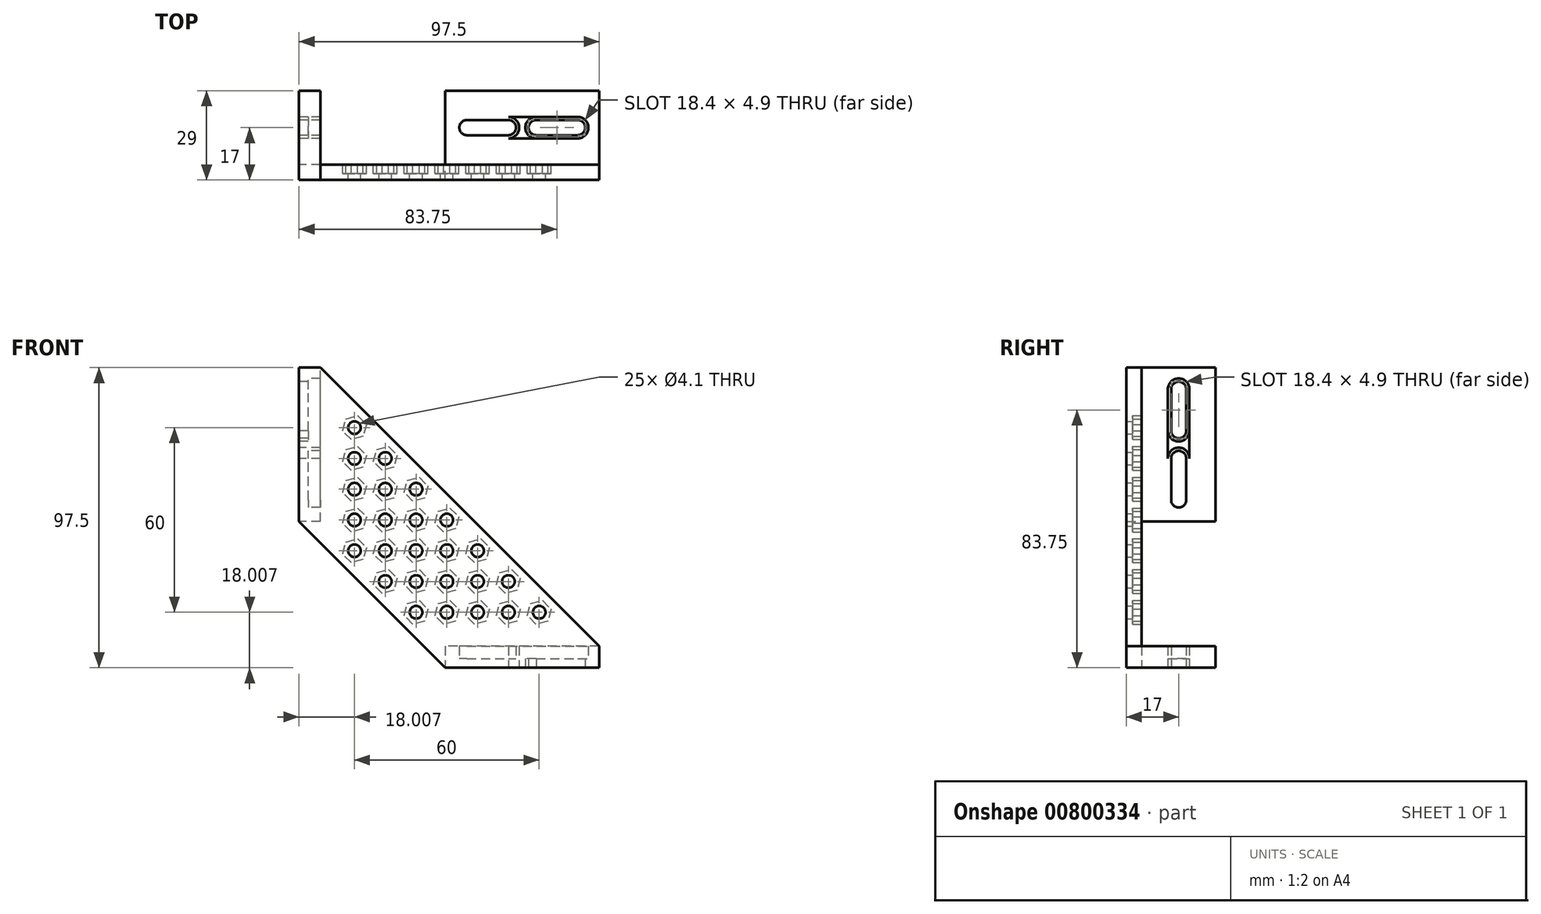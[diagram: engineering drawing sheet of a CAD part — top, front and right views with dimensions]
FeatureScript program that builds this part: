
annotation { "Feature Type Name" : "Feature", "Feature Type Description" : "" }
export const myFeature = defineFeature(function(context is Context, id is Id, definition is map)
    precondition{}
    {
        {
            var Q0;
            Q0=qCreatedBy(makeId("Top.planeOp"),FACE);
            var sketch = newSketch(context, id + "F0", { "sketchPlane" : qUnion([Q0])});
            skLineSegment(sketch, "E0.left", {"start": v(-21, 12) * mm, "end": v(-21, -12) * mm});
            skPoint(sketch, "E0.middle", {"position": v(0, 0) * mm});
            skLineSegment(sketch, "E1", {"start": v(-14, 12) * mm, "end": v(-14, -12) * mm, "construction": true});
            skPoint(sketch, "E2", {"position": v(-14, -8) * mm});
            skPoint(sketch, "E3", {"position": v(0, -8) * mm});
            skPoint(sketch, "E4", {"position": v(-14, 0) * mm});
            skArc(sketch, "E5", {"start": v(-14, -5.95) * mm, "mid": v(-16.05, -8) * mm, "end": v(-14, -10.05) * mm});
            skLineSegment(sketch, "E6", {"start": v(-14, -5.95) * mm, "end": v(0, -5.95) * mm});
            skLineSegment(sketch, "E7.MirrorCS", {"start": v(-14, -10.05) * mm, "end": v(0, -10.05) * mm});
            skArc(sketch, "E8", {"start": v(-14, -2.45) * mm, "mid": v(-16.45, 0) * mm, "end": v(-14, 2.45) * mm});
            skPoint(sketch, "E9.MirrorP", {"position": v(-14, 2.45) * mm});
            skLineSegment(sketch, "E10.MirrorCS", {"start": v(0, -12) * mm, "end": v(0, 12) * mm, "construction": true});
            skLineSegment(sketch, "E11", {"start": v(-21, -12) * mm, "end": v(0, -12) * mm});
            skLineSegment(sketch, "E12", {"start": v(-21, 0) * mm, "end": v(0, 0) * mm, "construction": true});
            skLineSegment(sketch, "E13", {"start": v(0, -8) * mm, "end": v(-21, -8) * mm, "construction": true});
            skPoint(sketch, "E13.endSnap0", {"position": v(-16.05, -8) * mm});
            skLineSegment(sketch, "E14", {"start": v(0, -12) * mm, "end": v(29, -12) * mm});
            skLineSegment(sketch, "E15", {"start": v(29, -12) * mm, "end": v(29, 12) * mm});
            skLineSegment(sketch, "E16", {"start": v(29, 12) * mm, "end": v(-21, 12) * mm});
            skLineSegment(sketch, "E17", {"start": v(22, 12) * mm, "end": v(22, -12) * mm, "construction": true});
            skLineSegment(sketch, "E18", {"start": v(0, -5.95) * mm, "end": v(22, -5.95) * mm});
            skLineSegment(sketch, "E19", {"start": v(0, -10.05) * mm, "end": v(22, -10.05) * mm});
            skLineSegment(sketch, "E20", {"start": v(22, 0) * mm, "end": v(0, 0) * mm, "construction": true});
            skLineSegment(sketch, "E21", {"start": v(0, -8) * mm, "end": v(22, -8) * mm, "construction": true});
            skArc(sketch, "E22", {"start": v(22, -2.45) * mm, "mid": v(24.45, 0) * mm, "end": v(22, 2.45) * mm});
            skArc(sketch, "E23", {"start": v(22, -10.05) * mm, "mid": v(24.05, -8) * mm, "end": v(22, -5.95) * mm});
            skLineSegment(sketch, "E24.MirrorCS", {"start": v(0, 5.95) * mm, "end": v(22, 5.95) * mm});
            skLineSegment(sketch, "E25.MirrorCS", {"start": v(0, 10.05) * mm, "end": v(22, 10.05) * mm});
            skLineSegment(sketch, "E26.MirrorCS", {"start": v(-14, 10.05) * mm, "end": v(0, 10.05) * mm});
            skLineSegment(sketch, "E27.MirrorCS", {"start": v(-14, 5.95) * mm, "end": v(0, 5.95) * mm});
            skArc(sketch, "E28.MirrorCS", {"start": v(-14, 5.95) * mm, "mid": v(-16.05, 8) * mm, "end": v(-14, 10.05) * mm});
            skArc(sketch, "E29.MirrorCS", {"start": v(22, 10.05) * mm, "mid": v(24.05, 8) * mm, "end": v(22, 5.95) * mm});
            skArc(sketch, "E30.0", {"start": v(-14, -4.5) * mm, "mid": v(-17.5, -8) * mm, "end": v(-14, -11.5) * mm});
            skLineSegment(sketch, "E30.1", {"start": v(4.6, -4.5) * mm, "end": v(22, -4.5) * mm});
            skArc(sketch, "E30.2", {"start": v(22, -11.5) * mm, "mid": v(25.5, -8) * mm, "end": v(22, -4.5) * mm});
            skLineSegment(sketch, "E30.3", {"start": v(-14, -4.5) * mm, "end": v(4.6, -4.5) * mm});
            skLineSegment(sketch, "E30.4", {"start": v(5, -11.5) * mm, "end": v(22, -11.5) * mm});
            skLineSegment(sketch, "E30.5", {"start": v(-14, -11.5) * mm, "end": v(5, -11.5) * mm});
            skArc(sketch, "E31.0", {"start": v(-14, 4.5) * mm, "mid": v(-17.5, 8) * mm, "end": v(-14, 11.5) * mm});
            skLineSegment(sketch, "E31.1", {"start": v(-3, 11.5) * mm, "end": v(22, 11.5) * mm});
            skArc(sketch, "E31.2", {"start": v(22, 11.5) * mm, "mid": v(25.5, 8) * mm, "end": v(22, 4.5) * mm});
            skLineSegment(sketch, "E31.3", {"start": v(-14, 11.5) * mm, "end": v(-3, 11.5) * mm});
            skLineSegment(sketch, "E31.4", {"start": v(-3, 4.5) * mm, "end": v(22, 4.5) * mm});
            skLineSegment(sketch, "E31.5", {"start": v(-14, 4.5) * mm, "end": v(-3, 4.5) * mm});
            skArc(sketch, "E32", {"start": v(-14, -3.5) * mm, "mid": v(-17.5, 0) * mm, "end": v(-14, 3.5) * mm});
            skArc(sketch, "E33", {"start": v(22, -3.5) * mm, "mid": v(25.5, 0) * mm, "end": v(22, 3.5) * mm});
            skLineSegment(sketch, "E34", {"start": v(-14, 3.5) * mm, "end": v(22, 3.5) * mm});
            skLineSegment(sketch, "E35", {"start": v(22, -3.5) * mm, "end": v(-14, -3.5) * mm});
            skPoint(sketch, "E36", {"position": v(29, 0) * mm});
            skLineSegment(sketch, "E37", {"start": v(-14, 2.45) * mm, "end": v(-0.5, 2.45) * mm});
            skPoint(sketch, "E38", {"position": v(-0.5, 0) * mm});
            skPoint(sketch, "E39", {"position": v(8.5, 0) * mm});
            skArc(sketch, "E40", {"start": v(-0.5, -2.45) * mm, "mid": v(1.95, 0) * mm, "end": v(-0.5, 2.45) * mm});
            skLineSegment(sketch, "E41", {"start": v(-14, -2.45) * mm, "end": v(-0.5, -2.45) * mm});
            skArc(sketch, "E42", {"start": v(8.5, -2.45) * mm, "mid": v(6.05, 0) * mm, "end": v(8.5, 2.45) * mm});
            skLineSegment(sketch, "E43", {"start": v(8.5, 2.45) * mm, "end": v(22, 2.45) * mm});
            skLineSegment(sketch, "E44", {"start": v(22, -2.45) * mm, "end": v(8.5, -2.45) * mm});
            skPoint(sketch, "E45", {"position": v(1.95, 0) * mm});
            skPoint(sketch, "E46", {"position": v(6.05, 0) * mm});
            skArc(sketch, "E47", {"start": v(-0.5, 3.5) * mm, "mid": v(3, 0) * mm, "end": v(-0.5, -3.5) * mm});
            skArc(sketch, "E48", {"start": v(8.5, 3.5) * mm, "mid": v(5, 0) * mm, "end": v(8.5, -3.5) * mm});
            skPoint(sketch, "E49", {"position": v(3, 0) * mm});
            skPoint(sketch, "E50", {"position": v(5, 0) * mm});
            skPoint(sketch, "E51", {"position": v(4, 3.5) * mm});
            skPoint(sketch, "E52", {"position": v(4, -3.5) * mm});
            skLineSegment(sketch, "E53", {"start": v(4, 12) * mm, "end": v(4, -12) * mm, "construction": true});
            skSolve(sketch);
        }
        {
            var Q0;
            Q0=makeQuery(id+"F0.imprint","IMPRINT",FACE,{"disambiguationData":[TD([[makeQuery(id+"F0.imprint","IMPRINT",EDGE,{"derivedFrom":sQuery(id+"F0.wireOp",EDGE,"E0.left")}),1.0]])]});
            var Q1;
            Q1=makeQuery(id+"F0.imprint","IMPRINT",FACE,{"disambiguationData":[TD([[makeQuery(id+"F0.imprint","IMPRINT",EDGE,{"derivedFrom":sQuery(id+"F0.wireOp",EDGE,"E5")}),1.0]])]});
            var Q2;
            Q2=makeQuery(id+"F0.imprint","IMPRINT",FACE,{"disambiguationData":[TD([[makeQuery(id+"F0.imprint","IMPRINT",EDGE,{"derivedFrom":sQuery(id+"F0.wireOp",EDGE,"E5")}),-1.0]])]});
            var Q3;
            Q3=makeQuery(id+"F0.imprint","IMPRINT",FACE,{"disambiguationData":[TD([[makeQuery(id+"F0.imprint","IMPRINT",EDGE,{"derivedFrom":sQuery(id+"F0.wireOp",EDGE,"E24.MirrorCS")}),-1.0]])]});
            var Q4;
            Q4=makeQuery(id+"F0.imprint","IMPRINT",FACE,{"disambiguationData":[TD([[makeQuery(id+"F0.imprint","IMPRINT",EDGE,{"derivedFrom":sQuery(id+"F0.wireOp",EDGE,"E24.MirrorCS")}),1.0]])]});
            var Q5;
            {var subQ0=sQuery(id+"F0.wireOp",EDGE,"E47");Q5=makeQuery(id+"F0.imprint","IMPRINT",FACE,{"disambiguationData":[TD([[makeQuery(id+"F0.imprint","IMPRINT",EDGE,{"derivedFrom":subQ0}),1.0]])]});}
            extrude(context, id + "F1", {"entities" : qUnion([Q0, Q1, Q2, Q3, Q4, Q5]), "depth" : 7 * mm, "offsetDistance" : 25 * mm});
        }
        {
            var Q0;
            Q0=makeQuery(id+"F0.imprint","IMPRINT",FACE,{"disambiguationData":[TD([[makeQuery(id+"F0.imprint","IMPRINT",EDGE,{"derivedFrom":sQuery(id+"F0.wireOp",EDGE,"E8")}),1.0]])]});
            var Q1;
            Q1=makeQuery(id+"F0.imprint","IMPRINT",FACE,{"disambiguationData":[TD([[makeQuery(id+"F0.imprint","IMPRINT",EDGE,{"derivedFrom":sQuery(id+"F0.wireOp",EDGE,"E22")}),-1.0]])]});
            extrude(context, id + "F2", {"entities" : qUnion([Q0, Q1]), "operationType" : NewBodyOperationType.ADD, "depth" : 3 * mm, "offsetDistance" : 25 * mm});
        }
        {
            var Q0;
            Q0=makeQuery(id+"F1.opExtrude","SWEPT_FACE",FACE,{"disambiguationData":[OSD([sQuery(id+"F0.wireOp",EDGE,"E0.left")])]});
            var sketch = newSketch(context, id + "F3", { "sketchPlane" : qUnion([Q0])});
            skLineSegment(sketch, "E54", {"start": v(-12, 3.5) * mm, "end": v(12, 3.5) * mm, "construction": true});
            skSolve(sketch);
        }
        {
            var Q0;
            Q0=makeQuery(id+"F1.opExtrude","SWEPT_BODY",BODY,{"disambiguationData":[OSD([sQuery(id+"F0.wireOp",EDGE,"E0.bottom"),sQuery(id+"F0.wireOp",EDGE,"E0.top"),sQuery(id+"F0.wireOp",EDGE,"E0.left"),sQuery(id+"F0.wireOp",EDGE,"E0.right"),sQuery(id+"F0.wireOp",EDGE,"rf366HtQ-3S43-huQP-rZQL-GLvETnePYKPt"),sQuery(id+"F0.wireOp",EDGE,"72d57c59-205e-4b86-9b7f-fefa83471a3c0.MirrorC"),sQuery(id+"F0.wireOp",EDGE,"3BxVGwLA-TLUy-tZVP-cH0U-NxRYkcQ5ksQi"),sQuery(id+"F0.wireOp",EDGE,"b526d6a5-a937-4610-9a53-f8e406b30c9d0.MirrorC"),sQuery(id+"F0.wireOp",EDGE,"71981b63-6e51-433c-862b-60b74b25135c0.MirrorC"),sQuery(id+"F0.wireOp",EDGE,"b5f8f83e-67df-48da-9f18-6f8bbd20fa1b0.MirrorC"),sQuery(id+"F0.wireOp",EDGE,"1DxgEhBs-8iCY-IMLj-HmtB-05ri525AO9wY"),sQuery(id+"F0.wireOp",EDGE,"NxLUD5A4-VjtB-lD8M-x3iM-VxBEk0lLSaKk"),sQuery(id+"F0.wireOp",EDGE,"3f1f5e11-1e70-4af8-87df-d7b5c765f6460.MirrorC")])]});
            var Q1;
            Q1=sQuery(id+"F3.wireOp",EDGE,"E54");
            transform(context, id + "F4", {"entities" : qUnion([Q0]), "transformType" : TransformType.ROTATION, "transformAxis" : qUnion([Q1]), "angle" : 90 * degree, "makeCopy" : true});
        }
        {
            var Q0;
            Q0=makeQuery(id+"F4.opPattern","COPY",FACE,{"derivedFrom":makeQuery(id+"F1.opExtrude","SWEPT_FACE",FACE,{"disambiguationData":[OSD([sQuery(id+"F0.wireOp",EDGE,"E0.left")])]}),"instanceName":"1"});
            var sketch = newSketch(context, id + "F5", { "sketchPlane" : qUnion([Q0])});
            skLineSegment(sketch, "E55", {"start": v(-21, -12) * mm, "end": v(-21, 12) * mm, "construction": true});
            skPoint(sketch, "E55.startSnap0", {"position": v(-21, -12) * mm});
            skSolve(sketch);
        }
        {
            var Q0;
            Q0=sQuery(id+"F5.wireOp",EDGE,"E55");
            cPlane(context, id + "F6", {"entities" : qUnion([Q0]), "cplaneType" : CPlaneType.LINE_ANGLE, "offset" : 25 * mm, "angle" : 90 * degree, "width" : 150 * mm, "height" : 150 * mm});
        }
        {
            var Q0;
            Q0=qCreatedBy(id+"F6.planeOp",FACE);
            var sketch = newSketch(context, id + "F7", { "sketchPlane" : qUnion([Q0])});
            skLineSegment(sketch, "E56", {"start": v(0, 3.5) * mm, "end": v(0, 53.5) * mm, "construction": true});
            skSolve(sketch);
        }
        {
            var Q0;
            Q0=makeQuery(id+"F4.opPattern","COPY",BODY,{"derivedFrom":makeQuery(id+"F1.opExtrude","SWEPT_BODY",BODY,{"disambiguationData":[OSD([sQuery(id+"F0.wireOp",EDGE,"E0.left"),sQuery(id+"F0.wireOp",EDGE,"E11"),sQuery(id+"F0.wireOp",EDGE,"E14"),sQuery(id+"F0.wireOp",EDGE,"E15"),sQuery(id+"F0.wireOp",EDGE,"E16"),sQuery(id+"F0.wireOp",EDGE,"2010bd3d-8bd0-4ab8-9feb-11eef9d441c0.0"),sQuery(id+"F0.wireOp",EDGE,"2010bd3d-8bd0-4ab8-9feb-11eef9d441c0.1"),sQuery(id+"F0.wireOp",EDGE,"2010bd3d-8bd0-4ab8-9feb-11eef9d441c0.2"),sQuery(id+"F0.wireOp",EDGE,"2010bd3d-8bd0-4ab8-9feb-11eef9d441c0.3"),sQuery(id+"F0.wireOp",EDGE,"2010bd3d-8bd0-4ab8-9feb-11eef9d441c0.4"),sQuery(id+"F0.wireOp",EDGE,"2010bd3d-8bd0-4ab8-9feb-11eef9d441c0.5")])]}),"instanceName":"1"});
            var Q1;
            Q1=sQuery(id+"F7.wireOp",EDGE,"E56");
            transform(context, id + "F8", {"entities" : qUnion([Q0]), "transformType" : TransformType.ROTATION, "transformAxis" : qUnion([Q1]), "angle" : 180 * degree, "makeCopy" : false});
        }
        {
            var Q0;
            Q0=makeQuery(id+"F4.opPattern","COPY",BODY,{"derivedFrom":makeQuery(id+"F1.opExtrude","SWEPT_BODY",BODY,{"disambiguationData":[OSD([sQuery(id+"F0.wireOp",EDGE,"E0.bottom"),sQuery(id+"F0.wireOp",EDGE,"E0.top"),sQuery(id+"F0.wireOp",EDGE,"E0.left"),sQuery(id+"F0.wireOp",EDGE,"E0.right"),sQuery(id+"F0.wireOp",EDGE,"rf366HtQ-3S43-huQP-rZQL-GLvETnePYKPt"),sQuery(id+"F0.wireOp",EDGE,"72d57c59-205e-4b86-9b7f-fefa83471a3c0.MirrorC"),sQuery(id+"F0.wireOp",EDGE,"3BxVGwLA-TLUy-tZVP-cH0U-NxRYkcQ5ksQi"),sQuery(id+"F0.wireOp",EDGE,"b526d6a5-a937-4610-9a53-f8e406b30c9d0.MirrorC"),sQuery(id+"F0.wireOp",EDGE,"71981b63-6e51-433c-862b-60b74b25135c0.MirrorC"),sQuery(id+"F0.wireOp",EDGE,"b5f8f83e-67df-48da-9f18-6f8bbd20fa1b0.MirrorC"),sQuery(id+"F0.wireOp",EDGE,"1DxgEhBs-8iCY-IMLj-HmtB-05ri525AO9wY"),sQuery(id+"F0.wireOp",EDGE,"NxLUD5A4-VjtB-lD8M-x3iM-VxBEk0lLSaKk"),sQuery(id+"F0.wireOp",EDGE,"3f1f5e11-1e70-4af8-87df-d7b5c765f6460.MirrorC")])]}),"instanceName":"1"});
            var Q1;
            Q1=qCreatedBy(makeId("Top.planeOp"),FACE);
            transform(context, id + "F9", {"entities" : qUnion([Q0]), "transformType" : TransformType.TRANSLATION_DISTANCE, "transformDirection" : qUnion([Q1]), "distance" : 44 * mm, "makeCopy" : false});
        }
        {
            var Q0;
            Q0=makeQuery(id+"F4.opPattern","COPY",BODY,{"derivedFrom":makeQuery(id+"F1.opExtrude","SWEPT_BODY",BODY,{"disambiguationData":[OSD([sQuery(id+"F0.wireOp",EDGE,"E0.bottom"),sQuery(id+"F0.wireOp",EDGE,"E0.top"),sQuery(id+"F0.wireOp",EDGE,"E0.left"),sQuery(id+"F0.wireOp",EDGE,"E0.right"),sQuery(id+"F0.wireOp",EDGE,"rf366HtQ-3S43-huQP-rZQL-GLvETnePYKPt"),sQuery(id+"F0.wireOp",EDGE,"72d57c59-205e-4b86-9b7f-fefa83471a3c0.MirrorC"),sQuery(id+"F0.wireOp",EDGE,"3BxVGwLA-TLUy-tZVP-cH0U-NxRYkcQ5ksQi"),sQuery(id+"F0.wireOp",EDGE,"b526d6a5-a937-4610-9a53-f8e406b30c9d0.MirrorC"),sQuery(id+"F0.wireOp",EDGE,"71981b63-6e51-433c-862b-60b74b25135c0.MirrorC"),sQuery(id+"F0.wireOp",EDGE,"b5f8f83e-67df-48da-9f18-6f8bbd20fa1b0.MirrorC"),sQuery(id+"F0.wireOp",EDGE,"1DxgEhBs-8iCY-IMLj-HmtB-05ri525AO9wY"),sQuery(id+"F0.wireOp",EDGE,"NxLUD5A4-VjtB-lD8M-x3iM-VxBEk0lLSaKk"),sQuery(id+"F0.wireOp",EDGE,"3f1f5e11-1e70-4af8-87df-d7b5c765f6460.MirrorC")])]}),"instanceName":"1"});
            var Q1;
            Q1=qCreatedBy(makeId("Right.planeOp"),FACE);
            transform(context, id + "F10", {"entities" : qUnion([Q0]), "transformType" : TransformType.TRANSLATION_DISTANCE, "transformDirection" : qUnion([Q1]), "distance" : 44 * mm, "oppositeDirection" : true, "makeCopy" : false});
        }
        {
            var Q0;
            Q0=sQuery(id+"F0.wireOp",VERTEX,"E0.left.end");
            var Q1;
            Q1=makeQuery(id+"F4.opPattern","COPY",VERTEX,{"derivedFrom":makeQuery(id+"F1.opExtrude","CAP_VERTEX",VERTEX,{"disambiguationData":[OSD([sQuery(id+"F0.wireOp",EDGE,"E0.left"),sQuery(id+"F0.wireOp",EDGE,"E16")])],"isStart":true}),"instanceName":"1"});
            var Q2;
            Q2=makeQuery(id+"F4.opPattern","COPY",VERTEX,{"derivedFrom":makeQuery(id+"F1.opExtrude","CAP_VERTEX",VERTEX,{"disambiguationData":[OSD([sQuery(id+"F0.wireOp",EDGE,"E0.left"),sQuery(id+"F0.wireOp",EDGE,"E16")])],"isStart":false}),"instanceName":"1"});
            cPlane(context, id + "F11", {"entities" : qUnion([Q0, Q1, Q2]), "cplaneType" : CPlaneType.THREE_POINT, "offset" : 25 * mm, "width" : 150 * mm, "height" : 150 * mm});
        }
        {
            var Q0;
            Q0=qCreatedBy(id+"F11.planeOp",FACE);
            var sketch = newSketch(context, id + "F12", { "sketchPlane" : qUnion([Q0])});
            skLineSegment(sketch, "E57", {"start": v(-21, 0) * mm, "end": v(-68.5, 47.5) * mm});
            skLineSegment(sketch, "E58", {"start": v(-61.5, 97.5) * mm, "end": v(29, 7) * mm});
            skLineSegment(sketch, "E59", {"start": v(-68.5, 47.5) * mm, "end": v(-68.5, 97.5) * mm});
            skLineSegment(sketch, "E60", {"start": v(-61.5, 97.5) * mm, "end": v(-68.5, 97.5) * mm});
            skLineSegment(sketch, "E61", {"start": v(-21, 0) * mm, "end": v(29, 0) * mm});
            skLineSegment(sketch, "E62", {"start": v(29, 0) * mm, "end": v(29, 7) * mm});
            skLineSegment(sketch, "E63", {"start": v(-68.5, 97.5) * mm, "end": v(-61.5, 97.5) * mm});
            skPoint(sketch, "E64", {"position": v(-20.5, 48) * mm});
            skCircle(sketch, "E65", {"center": v(-20.5, 48) * mm, "radius": 2.05 * mm});
            skCircle(sketch, "E66.cCircle", {"center": v(-20.5, 48) * mm, "radius": 4 * mm, "construction": true});
            skLineSegment(sketch, "E66.0", {"start": v(-23.32, 50.84) * mm, "end": v(-19.46, 51.87) * mm});
            skLineSegment(sketch, "E66.1", {"start": v(-19.46, 51.87) * mm, "end": v(-16.63, 49.04) * mm});
            skLineSegment(sketch, "E66.2", {"start": v(-16.63, 49.04) * mm, "end": v(-17.66, 45.18) * mm});
            skLineSegment(sketch, "E66.3", {"start": v(-17.66, 45.18) * mm, "end": v(-21.53, 44.14) * mm});
            skLineSegment(sketch, "E66.4", {"start": v(-21.53, 44.14) * mm, "end": v(-24.36, 46.97) * mm});
            skLineSegment(sketch, "E66.5", {"start": v(-24.36, 46.97) * mm, "end": v(-23.32, 50.84) * mm});
            skLineSegment(sketch, "E67", {"start": v(-44.75, 23.75) * mm, "end": v(-16.25, 52.25) * mm, "construction": true});
            skLineSegment(sketch, "E68", {"start": v(-68.5, 47.5) * mm, "end": v(-68.5, 0) * mm, "construction": true});
            skLineSegment(sketch, "E69", {"start": v(-68.5, 0) * mm, "end": v(-21, 0) * mm, "construction": true});
            skLineSegment(sketch, "E70", {"start": v(-21, 7) * mm, "end": v(-68.5, 7) * mm, "construction": true});
            skLineSegment(sketch, "E71", {"start": v(-68.5, 7) * mm, "end": v(-68.5, 47.5) * mm, "construction": true});
            skLineSegment(sketch, "E72", {"start": v(-53.5, 89.5) * mm, "end": v(-53.5, 15) * mm, "construction": true});
            skLineSegment(sketch, "E73", {"start": v(-53.5, 15) * mm, "end": v(21, 15) * mm, "construction": true});
            skPoint(sketch, "E74", {"position": v(-17.66, 50.84) * mm});
            skLineSegment(sketch, "E75", {"start": v(-20.5, 48) * mm, "end": v(-20.5, 15) * mm, "construction": true});
            skLineSegment(sketch, "E76", {"start": v(-20.5, 48) * mm, "end": v(-53.5, 48) * mm, "construction": true});
            skPoint(sketch, "E77", {"position": v(-20.5, 38) * mm});
            skCircle(sketch, "E78", {"center": v(-20.5, 38) * mm, "radius": 2.05 * mm});
            skCircle(sketch, "E79.cCircle", {"center": v(-20.5, 38) * mm, "radius": 4 * mm, "construction": true});
            skLineSegment(sketch, "E79.0", {"start": v(-23.32, 40.84) * mm, "end": v(-19.46, 41.87) * mm});
            skLineSegment(sketch, "E79.1", {"start": v(-19.46, 41.87) * mm, "end": v(-16.63, 39.04) * mm});
            skLineSegment(sketch, "E79.2", {"start": v(-16.63, 39.04) * mm, "end": v(-17.66, 35.18) * mm});
            skLineSegment(sketch, "E79.3", {"start": v(-17.66, 35.18) * mm, "end": v(-21.53, 34.14) * mm});
            skLineSegment(sketch, "E79.4", {"start": v(-21.53, 34.14) * mm, "end": v(-24.36, 36.97) * mm});
            skLineSegment(sketch, "E79.5", {"start": v(-24.36, 36.97) * mm, "end": v(-23.32, 40.84) * mm});
            skPoint(sketch, "E80", {"position": v(-30.5, 48) * mm});
            skCircle(sketch, "E81", {"center": v(-30.5, 48) * mm, "radius": 2.05 * mm});
            skCircle(sketch, "E82.cCircle", {"center": v(-30.5, 48) * mm, "radius": 4 * mm, "construction": true});
            skLineSegment(sketch, "E82.0", {"start": v(-33.32, 50.84) * mm, "end": v(-29.46, 51.87) * mm});
            skLineSegment(sketch, "E82.1", {"start": v(-29.46, 51.87) * mm, "end": v(-26.63, 49.04) * mm});
            skLineSegment(sketch, "E82.2", {"start": v(-26.63, 49.04) * mm, "end": v(-27.66, 45.18) * mm});
            skLineSegment(sketch, "E82.3", {"start": v(-27.66, 45.18) * mm, "end": v(-31.53, 44.14) * mm});
            skLineSegment(sketch, "E82.4", {"start": v(-31.53, 44.14) * mm, "end": v(-34.36, 46.97) * mm});
            skLineSegment(sketch, "E82.5", {"start": v(-34.36, 46.97) * mm, "end": v(-33.32, 50.84) * mm});
            skPoint(sketch, "E83", {"position": v(-30.5, 38) * mm});
            skCircle(sketch, "E84", {"center": v(-30.5, 38) * mm, "radius": 2.05 * mm});
            skCircle(sketch, "E85.cCircle", {"center": v(-30.5, 38) * mm, "radius": 4 * mm, "construction": true});
            skLineSegment(sketch, "E85.0", {"start": v(-33.32, 40.84) * mm, "end": v(-29.46, 41.87) * mm});
            skLineSegment(sketch, "E85.1", {"start": v(-29.46, 41.87) * mm, "end": v(-26.63, 39.04) * mm});
            skLineSegment(sketch, "E85.2", {"start": v(-26.63, 39.04) * mm, "end": v(-27.66, 35.18) * mm});
            skLineSegment(sketch, "E85.3", {"start": v(-27.66, 35.18) * mm, "end": v(-31.53, 34.14) * mm});
            skLineSegment(sketch, "E85.4", {"start": v(-31.53, 34.14) * mm, "end": v(-34.36, 36.97) * mm});
            skLineSegment(sketch, "E85.5", {"start": v(-34.36, 36.97) * mm, "end": v(-33.32, 40.84) * mm});
            skLineSegment(sketch, "E86", {"start": v(-20.5, 38) * mm, "end": v(-2, 38) * mm, "construction": true});
            skLineSegment(sketch, "E87", {"start": v(-30.5, 48) * mm, "end": v(-30.5, 66.5) * mm, "construction": true});
            skPoint(sketch, "E88", {"position": v(-10.5, 38) * mm});
            skCircle(sketch, "E89", {"center": v(-10.5, 38) * mm, "radius": 2.05 * mm});
            skCircle(sketch, "E90.cCircle", {"center": v(-10.5, 38) * mm, "radius": 4 * mm, "construction": true});
            skLineSegment(sketch, "E90.0", {"start": v(-13.32, 40.84) * mm, "end": v(-9.46, 41.87) * mm});
            skLineSegment(sketch, "E90.1", {"start": v(-9.46, 41.87) * mm, "end": v(-6.63, 39.04) * mm});
            skLineSegment(sketch, "E90.2", {"start": v(-6.63, 39.04) * mm, "end": v(-7.66, 35.18) * mm});
            skLineSegment(sketch, "E90.3", {"start": v(-7.66, 35.18) * mm, "end": v(-11.53, 34.14) * mm});
            skLineSegment(sketch, "E90.4", {"start": v(-11.53, 34.14) * mm, "end": v(-14.36, 36.97) * mm});
            skLineSegment(sketch, "E90.5", {"start": v(-14.36, 36.97) * mm, "end": v(-13.32, 40.84) * mm});
            skPoint(sketch, "E91", {"position": v(-30.5, 58) * mm});
            skCircle(sketch, "E92", {"center": v(-30.5, 58) * mm, "radius": 2.05 * mm});
            skCircle(sketch, "E93.cCircle", {"center": v(-30.5, 58) * mm, "radius": 4 * mm, "construction": true});
            skLineSegment(sketch, "E93.0", {"start": v(-33.32, 60.84) * mm, "end": v(-29.46, 61.87) * mm});
            skLineSegment(sketch, "E93.1", {"start": v(-29.46, 61.87) * mm, "end": v(-26.63, 59.04) * mm});
            skLineSegment(sketch, "E93.2", {"start": v(-26.63, 59.04) * mm, "end": v(-27.66, 55.18) * mm});
            skLineSegment(sketch, "E93.3", {"start": v(-27.66, 55.18) * mm, "end": v(-31.53, 54.14) * mm});
            skLineSegment(sketch, "E93.4", {"start": v(-31.53, 54.14) * mm, "end": v(-34.36, 56.97) * mm});
            skLineSegment(sketch, "E93.5", {"start": v(-34.36, 56.97) * mm, "end": v(-33.32, 60.84) * mm});
            skPoint(sketch, "E94", {"position": v(-40.5, 48) * mm});
            skCircle(sketch, "E95", {"center": v(-40.5, 48) * mm, "radius": 2.05 * mm});
            skCircle(sketch, "E96.cCircle", {"center": v(-40.5, 48) * mm, "radius": 4 * mm, "construction": true});
            skLineSegment(sketch, "E96.0", {"start": v(-43.32, 50.84) * mm, "end": v(-39.46, 51.87) * mm});
            skLineSegment(sketch, "E96.1", {"start": v(-39.46, 51.87) * mm, "end": v(-36.63, 49.04) * mm});
            skLineSegment(sketch, "E96.2", {"start": v(-36.63, 49.04) * mm, "end": v(-37.66, 45.18) * mm});
            skLineSegment(sketch, "E96.3", {"start": v(-37.66, 45.18) * mm, "end": v(-41.53, 44.14) * mm});
            skLineSegment(sketch, "E96.4", {"start": v(-41.53, 44.14) * mm, "end": v(-44.36, 46.97) * mm});
            skLineSegment(sketch, "E96.5", {"start": v(-44.36, 46.97) * mm, "end": v(-43.32, 50.84) * mm});
            skPoint(sketch, "E97", {"position": v(-40.5, 38) * mm});
            skCircle(sketch, "E98", {"center": v(-40.5, 38) * mm, "radius": 2.05 * mm});
            skCircle(sketch, "E99.cCircle", {"center": v(-40.5, 38) * mm, "radius": 4 * mm, "construction": true});
            skLineSegment(sketch, "E99.0", {"start": v(-43.32, 40.84) * mm, "end": v(-39.46, 41.87) * mm});
            skLineSegment(sketch, "E99.1", {"start": v(-39.46, 41.87) * mm, "end": v(-36.63, 39.04) * mm});
            skLineSegment(sketch, "E99.2", {"start": v(-36.63, 39.04) * mm, "end": v(-37.66, 35.18) * mm});
            skLineSegment(sketch, "E99.3", {"start": v(-37.66, 35.18) * mm, "end": v(-41.53, 34.14) * mm});
            skLineSegment(sketch, "E99.4", {"start": v(-41.53, 34.14) * mm, "end": v(-44.36, 36.97) * mm});
            skLineSegment(sketch, "E99.5", {"start": v(-44.36, 36.97) * mm, "end": v(-43.32, 40.84) * mm});
            skPoint(sketch, "E100", {"position": v(-40.5, 58) * mm});
            skCircle(sketch, "E101", {"center": v(-40.5, 58) * mm, "radius": 2.05 * mm});
            skCircle(sketch, "E102.cCircle", {"center": v(-40.5, 58) * mm, "radius": 4 * mm, "construction": true});
            skLineSegment(sketch, "E102.0", {"start": v(-43.32, 60.84) * mm, "end": v(-39.46, 61.87) * mm});
            skLineSegment(sketch, "E102.1", {"start": v(-39.46, 61.87) * mm, "end": v(-36.63, 59.04) * mm});
            skLineSegment(sketch, "E102.2", {"start": v(-36.63, 59.04) * mm, "end": v(-37.66, 55.18) * mm});
            skLineSegment(sketch, "E102.3", {"start": v(-37.66, 55.18) * mm, "end": v(-41.53, 54.14) * mm});
            skLineSegment(sketch, "E102.4", {"start": v(-41.53, 54.14) * mm, "end": v(-44.36, 56.97) * mm});
            skLineSegment(sketch, "E102.5", {"start": v(-44.36, 56.97) * mm, "end": v(-43.32, 60.84) * mm});
            skLineSegment(sketch, "E103", {"start": v(-40.5, 76.5) * mm, "end": v(-40.5, 28) * mm, "construction": true});
            skPoint(sketch, "E104", {"position": v(-20.5, 28) * mm});
            skCircle(sketch, "E105", {"center": v(-20.5, 28) * mm, "radius": 2.05 * mm});
            skCircle(sketch, "E106.cCircle", {"center": v(-20.5, 28) * mm, "radius": 4 * mm, "construction": true});
            skLineSegment(sketch, "E106.0", {"start": v(-23.32, 30.84) * mm, "end": v(-19.46, 31.87) * mm});
            skLineSegment(sketch, "E106.1", {"start": v(-19.46, 31.87) * mm, "end": v(-16.63, 29.04) * mm});
            skLineSegment(sketch, "E106.2", {"start": v(-16.63, 29.04) * mm, "end": v(-17.66, 25.18) * mm});
            skLineSegment(sketch, "E106.3", {"start": v(-17.66, 25.18) * mm, "end": v(-21.53, 24.14) * mm});
            skLineSegment(sketch, "E106.4", {"start": v(-21.53, 24.14) * mm, "end": v(-24.36, 26.97) * mm});
            skLineSegment(sketch, "E106.5", {"start": v(-24.36, 26.97) * mm, "end": v(-23.32, 30.84) * mm});
            skPoint(sketch, "E107", {"position": v(-30.5, 28) * mm});
            skCircle(sketch, "E108", {"center": v(-30.5, 28) * mm, "radius": 2.05 * mm});
            skCircle(sketch, "E109.cCircle", {"center": v(-30.5, 28) * mm, "radius": 4 * mm, "construction": true});
            skLineSegment(sketch, "E109.0", {"start": v(-33.32, 30.84) * mm, "end": v(-29.46, 31.87) * mm});
            skLineSegment(sketch, "E109.1", {"start": v(-29.46, 31.87) * mm, "end": v(-26.63, 29.04) * mm});
            skLineSegment(sketch, "E109.2", {"start": v(-26.63, 29.04) * mm, "end": v(-27.66, 25.18) * mm});
            skLineSegment(sketch, "E109.3", {"start": v(-27.66, 25.18) * mm, "end": v(-31.53, 24.14) * mm});
            skLineSegment(sketch, "E109.4", {"start": v(-31.53, 24.14) * mm, "end": v(-34.36, 26.97) * mm});
            skLineSegment(sketch, "E109.5", {"start": v(-34.36, 26.97) * mm, "end": v(-33.32, 30.84) * mm});
            skPoint(sketch, "E110", {"position": v(-10.5, 28) * mm});
            skCircle(sketch, "E111", {"center": v(-10.5, 28) * mm, "radius": 2.05 * mm});
            skCircle(sketch, "E112.cCircle", {"center": v(-10.5, 28) * mm, "radius": 4 * mm, "construction": true});
            skLineSegment(sketch, "E112.0", {"start": v(-13.32, 30.84) * mm, "end": v(-9.46, 31.87) * mm});
            skLineSegment(sketch, "E112.1", {"start": v(-9.46, 31.87) * mm, "end": v(-6.63, 29.04) * mm});
            skLineSegment(sketch, "E112.2", {"start": v(-6.63, 29.04) * mm, "end": v(-7.66, 25.18) * mm});
            skLineSegment(sketch, "E112.3", {"start": v(-7.66, 25.18) * mm, "end": v(-11.53, 24.14) * mm});
            skLineSegment(sketch, "E112.4", {"start": v(-11.53, 24.14) * mm, "end": v(-14.36, 26.97) * mm});
            skLineSegment(sketch, "E112.5", {"start": v(-14.36, 26.97) * mm, "end": v(-13.32, 30.84) * mm});
            skPoint(sketch, "E113", {"position": v(-40.5, 28) * mm});
            skCircle(sketch, "E114", {"center": v(-40.5, 28) * mm, "radius": 2.05 * mm});
            skCircle(sketch, "E115.cCircle", {"center": v(-40.5, 28) * mm, "radius": 4 * mm, "construction": true});
            skLineSegment(sketch, "E115.0", {"start": v(-43.32, 30.84) * mm, "end": v(-39.46, 31.87) * mm});
            skLineSegment(sketch, "E115.1", {"start": v(-39.46, 31.87) * mm, "end": v(-36.63, 29.04) * mm});
            skLineSegment(sketch, "E115.2", {"start": v(-36.63, 29.04) * mm, "end": v(-37.66, 25.18) * mm});
            skLineSegment(sketch, "E115.3", {"start": v(-37.66, 25.18) * mm, "end": v(-41.53, 24.14) * mm});
            skLineSegment(sketch, "E115.4", {"start": v(-41.53, 24.14) * mm, "end": v(-44.36, 26.97) * mm});
            skLineSegment(sketch, "E115.5", {"start": v(-44.36, 26.97) * mm, "end": v(-43.32, 30.84) * mm});
            skLineSegment(sketch, "E116", {"start": v(8, 28) * mm, "end": v(-40.5, 28) * mm, "construction": true});
            skPoint(sketch, "E117", {"position": v(-40.5, 68) * mm});
            skCircle(sketch, "E118", {"center": v(-40.5, 68) * mm, "radius": 2.05 * mm});
            skCircle(sketch, "E119.cCircle", {"center": v(-40.5, 68) * mm, "radius": 4 * mm, "construction": true});
            skLineSegment(sketch, "E119.0", {"start": v(-44.36, 66.97) * mm, "end": v(-43.32, 70.84) * mm});
            skLineSegment(sketch, "E119.1", {"start": v(-43.32, 70.84) * mm, "end": v(-39.46, 71.87) * mm});
            skLineSegment(sketch, "E119.2", {"start": v(-39.46, 71.87) * mm, "end": v(-36.63, 69.04) * mm});
            skLineSegment(sketch, "E119.3", {"start": v(-36.63, 69.04) * mm, "end": v(-37.66, 65.18) * mm});
            skLineSegment(sketch, "E119.4", {"start": v(-37.66, 65.18) * mm, "end": v(-41.53, 64.14) * mm});
            skLineSegment(sketch, "E119.5", {"start": v(-41.53, 64.14) * mm, "end": v(-44.36, 66.97) * mm});
            skPoint(sketch, "E120", {"position": v(-0.5, 28) * mm});
            skCircle(sketch, "E121", {"center": v(-0.5, 28) * mm, "radius": 2.05 * mm});
            skCircle(sketch, "E122.cCircle", {"center": v(-0.5, 28) * mm, "radius": 4 * mm, "construction": true});
            skLineSegment(sketch, "E122.0", {"start": v(-3.32, 30.84) * mm, "end": v(0.54, 31.87) * mm});
            skLineSegment(sketch, "E122.1", {"start": v(0.54, 31.87) * mm, "end": v(3.37, 29.04) * mm});
            skLineSegment(sketch, "E122.2", {"start": v(3.37, 29.04) * mm, "end": v(2.34, 25.18) * mm});
            skLineSegment(sketch, "E122.3", {"start": v(2.34, 25.18) * mm, "end": v(-1.53, 24.14) * mm});
            skLineSegment(sketch, "E122.4", {"start": v(-1.53, 24.14) * mm, "end": v(-4.36, 26.97) * mm});
            skLineSegment(sketch, "E122.5", {"start": v(-4.36, 26.97) * mm, "end": v(-3.32, 30.84) * mm});
            skPoint(sketch, "E123", {"position": v(-10.5, 18) * mm});
            skCircle(sketch, "E124", {"center": v(-10.5, 18) * mm, "radius": 2.05 * mm});
            skCircle(sketch, "E125.cCircle", {"center": v(-10.5, 18) * mm, "radius": 4 * mm, "construction": true});
            skLineSegment(sketch, "E125.0", {"start": v(-13.32, 20.84) * mm, "end": v(-9.46, 21.87) * mm});
            skLineSegment(sketch, "E125.1", {"start": v(-9.46, 21.87) * mm, "end": v(-6.63, 19.04) * mm});
            skLineSegment(sketch, "E125.2", {"start": v(-6.63, 19.04) * mm, "end": v(-7.66, 15.18) * mm});
            skLineSegment(sketch, "E125.3", {"start": v(-7.66, 15.18) * mm, "end": v(-11.53, 14.14) * mm});
            skLineSegment(sketch, "E125.4", {"start": v(-11.53, 14.14) * mm, "end": v(-14.36, 16.97) * mm});
            skLineSegment(sketch, "E125.5", {"start": v(-14.36, 16.97) * mm, "end": v(-13.32, 20.84) * mm});
            skPoint(sketch, "E126", {"position": v(-20.5, 18) * mm});
            skCircle(sketch, "E127", {"center": v(-20.5, 18) * mm, "radius": 2.05 * mm});
            skCircle(sketch, "E128.cCircle", {"center": v(-20.5, 18) * mm, "radius": 4 * mm, "construction": true});
            skLineSegment(sketch, "E128.0", {"start": v(-23.32, 20.84) * mm, "end": v(-19.46, 21.87) * mm});
            skLineSegment(sketch, "E128.1", {"start": v(-19.46, 21.87) * mm, "end": v(-16.63, 19.04) * mm});
            skLineSegment(sketch, "E128.2", {"start": v(-16.63, 19.04) * mm, "end": v(-17.66, 15.18) * mm});
            skLineSegment(sketch, "E128.3", {"start": v(-17.66, 15.18) * mm, "end": v(-21.53, 14.14) * mm});
            skLineSegment(sketch, "E128.4", {"start": v(-21.53, 14.14) * mm, "end": v(-24.36, 16.97) * mm});
            skLineSegment(sketch, "E128.5", {"start": v(-24.36, 16.97) * mm, "end": v(-23.32, 20.84) * mm});
            skPoint(sketch, "E129", {"position": v(-0.5, 18) * mm});
            skCircle(sketch, "E130", {"center": v(-0.5, 18) * mm, "radius": 2.05 * mm});
            skCircle(sketch, "E131.cCircle", {"center": v(-0.5, 18) * mm, "radius": 4 * mm, "construction": true});
            skLineSegment(sketch, "E131.0", {"start": v(-3.32, 20.84) * mm, "end": v(0.54, 21.87) * mm});
            skLineSegment(sketch, "E131.1", {"start": v(0.54, 21.87) * mm, "end": v(3.37, 19.04) * mm});
            skLineSegment(sketch, "E131.2", {"start": v(3.37, 19.04) * mm, "end": v(2.34, 15.18) * mm});
            skLineSegment(sketch, "E131.3", {"start": v(2.34, 15.18) * mm, "end": v(-1.53, 14.14) * mm});
            skLineSegment(sketch, "E131.4", {"start": v(-1.53, 14.14) * mm, "end": v(-4.36, 16.97) * mm});
            skLineSegment(sketch, "E131.5", {"start": v(-4.36, 16.97) * mm, "end": v(-3.32, 20.84) * mm});
            skPoint(sketch, "E132", {"position": v(-30.5, 18) * mm});
            skCircle(sketch, "E133", {"center": v(-30.5, 18) * mm, "radius": 2.05 * mm});
            skCircle(sketch, "E134.cCircle", {"center": v(-30.5, 18) * mm, "radius": 4 * mm, "construction": true});
            skLineSegment(sketch, "E134.0", {"start": v(-33.32, 20.84) * mm, "end": v(-29.46, 21.87) * mm});
            skLineSegment(sketch, "E134.1", {"start": v(-29.46, 21.87) * mm, "end": v(-26.63, 19.04) * mm});
            skLineSegment(sketch, "E134.2", {"start": v(-26.63, 19.04) * mm, "end": v(-27.66, 15.18) * mm});
            skLineSegment(sketch, "E134.3", {"start": v(-27.66, 15.18) * mm, "end": v(-31.53, 14.14) * mm});
            skLineSegment(sketch, "E134.4", {"start": v(-31.53, 14.14) * mm, "end": v(-34.36, 16.97) * mm});
            skLineSegment(sketch, "E134.5", {"start": v(-34.36, 16.97) * mm, "end": v(-33.32, 20.84) * mm});
            skLineSegment(sketch, "E135", {"start": v(18, 18) * mm, "end": v(-39, 18) * mm, "construction": true});
            skPoint(sketch, "E136", {"position": v(9.5, 18) * mm});
            skCircle(sketch, "E137", {"center": v(9.5, 18) * mm, "radius": 2.05 * mm});
            skCircle(sketch, "E138.cCircle", {"center": v(9.5, 18) * mm, "radius": 4 * mm, "construction": true});
            skLineSegment(sketch, "E138.0", {"start": v(5.64, 16.97) * mm, "end": v(6.68, 20.84) * mm});
            skLineSegment(sketch, "E138.1", {"start": v(6.68, 20.84) * mm, "end": v(10.54, 21.87) * mm});
            skLineSegment(sketch, "E138.2", {"start": v(10.54, 21.87) * mm, "end": v(13.37, 19.04) * mm});
            skLineSegment(sketch, "E138.3", {"start": v(13.37, 19.04) * mm, "end": v(12.34, 15.18) * mm});
            skLineSegment(sketch, "E138.4", {"start": v(12.34, 15.18) * mm, "end": v(8.47, 14.14) * mm});
            skLineSegment(sketch, "E138.5", {"start": v(8.47, 14.14) * mm, "end": v(5.64, 16.97) * mm});
            skPoint(sketch, "E139", {"position": v(-50.5, 58) * mm});
            skCircle(sketch, "E140", {"center": v(-50.5, 58) * mm, "radius": 2.05 * mm});
            skCircle(sketch, "E141.cCircle", {"center": v(-50.5, 58) * mm, "radius": 4 * mm, "construction": true});
            skLineSegment(sketch, "E141.0", {"start": v(-53.32, 60.84) * mm, "end": v(-49.46, 61.87) * mm});
            skLineSegment(sketch, "E141.1", {"start": v(-49.46, 61.87) * mm, "end": v(-46.63, 59.04) * mm});
            skLineSegment(sketch, "E141.2", {"start": v(-46.63, 59.04) * mm, "end": v(-47.66, 55.18) * mm});
            skLineSegment(sketch, "E141.3", {"start": v(-47.66, 55.18) * mm, "end": v(-51.53, 54.14) * mm});
            skLineSegment(sketch, "E141.4", {"start": v(-51.53, 54.14) * mm, "end": v(-54.36, 56.97) * mm});
            skLineSegment(sketch, "E141.5", {"start": v(-54.36, 56.97) * mm, "end": v(-53.32, 60.84) * mm});
            skPoint(sketch, "E142", {"position": v(-50.5, 48) * mm});
            skCircle(sketch, "E143", {"center": v(-50.5, 48) * mm, "radius": 2.05 * mm});
            skCircle(sketch, "E144.cCircle", {"center": v(-50.5, 48) * mm, "radius": 4 * mm, "construction": true});
            skLineSegment(sketch, "E144.0", {"start": v(-53.32, 50.84) * mm, "end": v(-49.46, 51.87) * mm});
            skLineSegment(sketch, "E144.1", {"start": v(-49.46, 51.87) * mm, "end": v(-46.63, 49.04) * mm});
            skLineSegment(sketch, "E144.2", {"start": v(-46.63, 49.04) * mm, "end": v(-47.66, 45.18) * mm});
            skLineSegment(sketch, "E144.3", {"start": v(-47.66, 45.18) * mm, "end": v(-51.53, 44.14) * mm});
            skLineSegment(sketch, "E144.4", {"start": v(-51.53, 44.14) * mm, "end": v(-54.36, 46.97) * mm});
            skLineSegment(sketch, "E144.5", {"start": v(-54.36, 46.97) * mm, "end": v(-53.32, 50.84) * mm});
            skPoint(sketch, "E145", {"position": v(-50.5, 68) * mm});
            skCircle(sketch, "E146", {"center": v(-50.5, 68) * mm, "radius": 2.05 * mm});
            skCircle(sketch, "E147.cCircle", {"center": v(-50.5, 68) * mm, "radius": 4 * mm, "construction": true});
            skLineSegment(sketch, "E147.0", {"start": v(-53.32, 70.84) * mm, "end": v(-49.46, 71.87) * mm});
            skLineSegment(sketch, "E147.1", {"start": v(-49.46, 71.87) * mm, "end": v(-46.63, 69.04) * mm});
            skLineSegment(sketch, "E147.2", {"start": v(-46.63, 69.04) * mm, "end": v(-47.66, 65.18) * mm});
            skLineSegment(sketch, "E147.3", {"start": v(-47.66, 65.18) * mm, "end": v(-51.53, 64.14) * mm});
            skLineSegment(sketch, "E147.4", {"start": v(-51.53, 64.14) * mm, "end": v(-54.36, 66.97) * mm});
            skLineSegment(sketch, "E147.5", {"start": v(-54.36, 66.97) * mm, "end": v(-53.32, 70.84) * mm});
            skPoint(sketch, "E148", {"position": v(-50.5, 38) * mm});
            skCircle(sketch, "E149", {"center": v(-50.5, 38) * mm, "radius": 2.05 * mm});
            skCircle(sketch, "E150.cCircle", {"center": v(-50.5, 38) * mm, "radius": 4 * mm, "construction": true});
            skLineSegment(sketch, "E150.0", {"start": v(-53.32, 40.84) * mm, "end": v(-49.46, 41.87) * mm});
            skLineSegment(sketch, "E150.1", {"start": v(-49.46, 41.87) * mm, "end": v(-46.63, 39.04) * mm});
            skLineSegment(sketch, "E150.2", {"start": v(-46.63, 39.04) * mm, "end": v(-47.66, 35.18) * mm});
            skLineSegment(sketch, "E150.3", {"start": v(-47.66, 35.18) * mm, "end": v(-51.53, 34.14) * mm});
            skLineSegment(sketch, "E150.4", {"start": v(-51.53, 34.14) * mm, "end": v(-54.36, 36.97) * mm});
            skLineSegment(sketch, "E150.5", {"start": v(-54.36, 36.97) * mm, "end": v(-53.32, 40.84) * mm});
            skPoint(sketch, "E151", {"position": v(-50.5, 78) * mm});
            skCircle(sketch, "E152", {"center": v(-50.5, 78) * mm, "radius": 2.05 * mm});
            skCircle(sketch, "E153.cCircle", {"center": v(-50.5, 78) * mm, "radius": 4 * mm, "construction": true});
            skLineSegment(sketch, "E153.0", {"start": v(-54.36, 76.97) * mm, "end": v(-53.32, 80.84) * mm});
            skLineSegment(sketch, "E153.1", {"start": v(-53.32, 80.84) * mm, "end": v(-49.46, 81.87) * mm});
            skLineSegment(sketch, "E153.2", {"start": v(-49.46, 81.87) * mm, "end": v(-46.63, 79.04) * mm});
            skLineSegment(sketch, "E153.3", {"start": v(-46.63, 79.04) * mm, "end": v(-47.66, 75.18) * mm});
            skLineSegment(sketch, "E153.4", {"start": v(-47.66, 75.18) * mm, "end": v(-51.53, 74.14) * mm});
            skLineSegment(sketch, "E153.5", {"start": v(-51.53, 74.14) * mm, "end": v(-54.36, 76.97) * mm});
            skLineSegment(sketch, "E154", {"start": v(-50.5, 86.5) * mm, "end": v(-50.5, 29.5) * mm, "construction": true});
            skSolve(sketch);
        }
        {
            var Q0;
            Q0=makeQuery(id+"F12.imprint","IMPRINT",FACE,{"disambiguationData":[TD([[makeQuery(id+"F12.imprint","IMPRINT",EDGE,{"derivedFrom":sQuery(id+"F12.wireOp",EDGE,"E58")}),-1.0]])]});
            var Q1;
            Q1=makeQuery(id+"F12.imprint","IMPRINT",FACE,{"disambiguationData":[TD([[makeQuery(id+"F12.imprint","IMPRINT",EDGE,{"derivedFrom":sQuery(id+"F12.wireOp",EDGE,"544cc5c5-56e9-462e-aa7d-0e891712fb88")}),-1.0]])]});
            var Q2;
            Q2=makeQuery(id+"F12.imprint","IMPRINT",FACE,{"disambiguationData":[TD([[makeQuery(id+"F12.imprint","IMPRINT",EDGE,{"derivedFrom":sQuery(id+"F12.wireOp",EDGE,"af930993-f983-4d4b-806c-d5d714f01deb")}),-1.0]])]});
            var Q3;
            Q3=makeQuery(id+"F12.imprint","IMPRINT",FACE,{"disambiguationData":[TD([[makeQuery(id+"F12.imprint","IMPRINT",EDGE,{"derivedFrom":sQuery(id+"F12.wireOp",EDGE,"E65")}),-1.0]])]});
            var Q4;
            Q4=makeQuery(id+"F12.imprint","IMPRINT",FACE,{"disambiguationData":[TD([[makeQuery(id+"F12.imprint","IMPRINT",EDGE,{"derivedFrom":sQuery(id+"F12.wireOp",EDGE,"db4000d2-28b7-4ce0-b6f8-efe2c8e47721")}),-1.0]])]});
            var Q5;
            Q5=makeQuery(id+"F12.imprint","IMPRINT",FACE,{"disambiguationData":[TD([[makeQuery(id+"F12.imprint","IMPRINT",EDGE,{"derivedFrom":sQuery(id+"F12.wireOp",EDGE,"6fd45c98-9014-41e2-a4b9-07c20c1fc8f4")}),-1.0]])]});
            var Q6;
            {var subQ0=sQuery(id+"F12.wireOp",EDGE,"36f95dd1-a930-4b05-802e-2328d4aa170c.1");Q6=makeQuery(id+"F12.imprint","IMPRINT",FACE,{"disambiguationData":[TD([[makeQuery(id+"F12.imprint","IMPRINT",EDGE,{"derivedFrom":subQ0}),-1.0]])]});}
            var Q7;
            Q7=makeQuery(id+"F12.imprint","IMPRINT",FACE,{"disambiguationData":[TD([[makeQuery(id+"F12.imprint","IMPRINT",EDGE,{"derivedFrom":sQuery(id+"F12.wireOp",EDGE,"0217be3f-f015-4376-87de-3fac7a7125e00.MirrorCS")}),1.0]])]});
            var Q8;
            Q8=makeQuery(id+"F12.imprint","IMPRINT",FACE,{"disambiguationData":[TD([[makeQuery(id+"F12.imprint","IMPRINT",EDGE,{"derivedFrom":sQuery(id+"F12.wireOp",EDGE,"3a05cbfe-0b2f-41ad-9fce-b7c3e8f461170.MirrorCS")}),1.0]])]});
            var Q9;
            Q9=makeQuery(id+"F12.imprint","IMPRINT",FACE,{"disambiguationData":[TD([[makeQuery(id+"F12.imprint","IMPRINT",EDGE,{"derivedFrom":sQuery(id+"F12.wireOp",EDGE,"686798c7-8504-4800-9966-571d6854760d0.MirrorCS")}),1.0]])]});
            var Q10;
            Q10=makeQuery(id+"F12.imprint","IMPRINT",FACE,{"disambiguationData":[TD([[makeQuery(id+"F12.imprint","IMPRINT",EDGE,{"derivedFrom":sQuery(id+"F12.wireOp",EDGE,"ee1293b9-60a1-4feb-baa6-848b5ec06ea80.MirrorCS")}),1.0]])]});
            var Q11;
            Q11=makeQuery(id+"F12.imprint","IMPRINT",FACE,{"disambiguationData":[TD([[makeQuery(id+"F12.imprint","IMPRINT",EDGE,{"derivedFrom":sQuery(id+"F12.wireOp",EDGE,"E92")}),-1.0]])]});
            var Q12;
            Q12=makeQuery(id+"F12.imprint","IMPRINT",FACE,{"disambiguationData":[TD([[makeQuery(id+"F12.imprint","IMPRINT",EDGE,{"derivedFrom":sQuery(id+"F12.wireOp",EDGE,"E81")}),-1.0]])]});
            var Q13;
            Q13=makeQuery(id+"F12.imprint","IMPRINT",FACE,{"disambiguationData":[TD([[makeQuery(id+"F12.imprint","IMPRINT",EDGE,{"derivedFrom":sQuery(id+"F12.wireOp",EDGE,"E84")}),-1.0]])]});
            var Q14;
            Q14=makeQuery(id+"F12.imprint","IMPRINT",FACE,{"disambiguationData":[TD([[makeQuery(id+"F12.imprint","IMPRINT",EDGE,{"derivedFrom":sQuery(id+"F12.wireOp",EDGE,"E78")}),-1.0]])]});
            var Q15;
            Q15=makeQuery(id+"F12.imprint","IMPRINT",FACE,{"disambiguationData":[TD([[makeQuery(id+"F12.imprint","IMPRINT",EDGE,{"derivedFrom":sQuery(id+"F12.wireOp",EDGE,"E89")}),-1.0]])]});
            var Q16;
            Q16=makeQuery(id+"F12.imprint","IMPRINT",FACE,{"disambiguationData":[TD([[makeQuery(id+"F12.imprint","IMPRINT",EDGE,{"derivedFrom":sQuery(id+"F12.wireOp",EDGE,"E118")}),-1.0]])]});
            var Q17;
            Q17=makeQuery(id+"F12.imprint","IMPRINT",FACE,{"disambiguationData":[TD([[makeQuery(id+"F12.imprint","IMPRINT",EDGE,{"derivedFrom":sQuery(id+"F12.wireOp",EDGE,"E101")}),-1.0]])]});
            var Q18;
            Q18=makeQuery(id+"F12.imprint","IMPRINT",FACE,{"disambiguationData":[TD([[makeQuery(id+"F12.imprint","IMPRINT",EDGE,{"derivedFrom":sQuery(id+"F12.wireOp",EDGE,"E95")}),-1.0]])]});
            var Q19;
            Q19=makeQuery(id+"F12.imprint","IMPRINT",FACE,{"disambiguationData":[TD([[makeQuery(id+"F12.imprint","IMPRINT",EDGE,{"derivedFrom":sQuery(id+"F12.wireOp",EDGE,"E98")}),-1.0]])]});
            var Q20;
            Q20=makeQuery(id+"F12.imprint","IMPRINT",FACE,{"disambiguationData":[TD([[makeQuery(id+"F12.imprint","IMPRINT",EDGE,{"derivedFrom":sQuery(id+"F12.wireOp",EDGE,"E114")}),-1.0]])]});
            var Q21;
            Q21=makeQuery(id+"F12.imprint","IMPRINT",FACE,{"disambiguationData":[TD([[makeQuery(id+"F12.imprint","IMPRINT",EDGE,{"derivedFrom":sQuery(id+"F12.wireOp",EDGE,"E108")}),-1.0]])]});
            var Q22;
            Q22=makeQuery(id+"F12.imprint","IMPRINT",FACE,{"disambiguationData":[TD([[makeQuery(id+"F12.imprint","IMPRINT",EDGE,{"derivedFrom":sQuery(id+"F12.wireOp",EDGE,"E105")}),-1.0]])]});
            var Q23;
            Q23=makeQuery(id+"F12.imprint","IMPRINT",FACE,{"disambiguationData":[TD([[makeQuery(id+"F12.imprint","IMPRINT",EDGE,{"derivedFrom":sQuery(id+"F12.wireOp",EDGE,"E111")}),-1.0]])]});
            var Q24;
            Q24=makeQuery(id+"F12.imprint","IMPRINT",FACE,{"disambiguationData":[TD([[makeQuery(id+"F12.imprint","IMPRINT",EDGE,{"derivedFrom":sQuery(id+"F12.wireOp",EDGE,"E121")}),-1.0]])]});
            var Q25;
            Q25=makeQuery(id+"F12.imprint","IMPRINT",FACE,{"disambiguationData":[TD([[makeQuery(id+"F12.imprint","IMPRINT",EDGE,{"derivedFrom":sQuery(id+"F12.wireOp",EDGE,"E140")}),-1.0]])]});
            var Q26;
            Q26=makeQuery(id+"F12.imprint","IMPRINT",FACE,{"disambiguationData":[TD([[makeQuery(id+"F12.imprint","IMPRINT",EDGE,{"derivedFrom":sQuery(id+"F12.wireOp",EDGE,"E146")}),-1.0]])]});
            var Q27;
            Q27=makeQuery(id+"F12.imprint","IMPRINT",FACE,{"disambiguationData":[TD([[makeQuery(id+"F12.imprint","IMPRINT",EDGE,{"derivedFrom":sQuery(id+"F12.wireOp",EDGE,"E152")}),-1.0]])]});
            var Q28;
            Q28=makeQuery(id+"F12.imprint","IMPRINT",FACE,{"disambiguationData":[TD([[makeQuery(id+"F12.imprint","IMPRINT",EDGE,{"derivedFrom":sQuery(id+"F12.wireOp",EDGE,"E143")}),-1.0]])]});
            var Q29;
            Q29=makeQuery(id+"F12.imprint","IMPRINT",FACE,{"disambiguationData":[TD([[makeQuery(id+"F12.imprint","IMPRINT",EDGE,{"derivedFrom":sQuery(id+"F12.wireOp",EDGE,"E149")}),-1.0]])]});
            var Q30;
            Q30=makeQuery(id+"F12.imprint","IMPRINT",FACE,{"disambiguationData":[TD([[makeQuery(id+"F12.imprint","IMPRINT",EDGE,{"derivedFrom":sQuery(id+"F12.wireOp",EDGE,"E133")}),-1.0]])]});
            var Q31;
            Q31=makeQuery(id+"F12.imprint","IMPRINT",FACE,{"disambiguationData":[TD([[makeQuery(id+"F12.imprint","IMPRINT",EDGE,{"derivedFrom":sQuery(id+"F12.wireOp",EDGE,"E127")}),-1.0]])]});
            var Q32;
            Q32=makeQuery(id+"F12.imprint","IMPRINT",FACE,{"disambiguationData":[TD([[makeQuery(id+"F12.imprint","IMPRINT",EDGE,{"derivedFrom":sQuery(id+"F12.wireOp",EDGE,"E124")}),-1.0]])]});
            var Q33;
            Q33=makeQuery(id+"F12.imprint","IMPRINT",FACE,{"disambiguationData":[TD([[makeQuery(id+"F12.imprint","IMPRINT",EDGE,{"derivedFrom":sQuery(id+"F12.wireOp",EDGE,"E130")}),-1.0]])]});
            var Q34;
            Q34=makeQuery(id+"F12.imprint","IMPRINT",FACE,{"disambiguationData":[TD([[makeQuery(id+"F12.imprint","IMPRINT",EDGE,{"derivedFrom":sQuery(id+"F12.wireOp",EDGE,"E137")}),-1.0]])]});
            extrude(context, id + "F13", {"entities" : qUnion([Q0, Q1, Q2, Q3, Q4, Q5, Q6, Q7, Q8, Q9, Q10, Q11, Q12, Q13, Q14, Q15, Q16, Q17, Q18, Q19, Q20, Q21, Q22, Q23, Q24, Q25, Q26, Q27, Q28, Q29, Q30, Q31, Q32, Q33, Q34]), "operationType" : NewBodyOperationType.ADD, "depth" : 5 * mm, "offsetDistance" : 25 * mm});
        }
        {
            var Q0;
            Q0=makeQuery(id+"F12.imprint","IMPRINT",FACE,{"disambiguationData":[TD([[makeQuery(id+"F12.imprint","IMPRINT",EDGE,{"derivedFrom":sQuery(id+"F12.wireOp",EDGE,"E65")}),-1.0]])]});
            var Q1;
            Q1=makeQuery(id+"F12.imprint","IMPRINT",FACE,{"disambiguationData":[TD([[makeQuery(id+"F12.imprint","IMPRINT",EDGE,{"derivedFrom":sQuery(id+"F12.wireOp",EDGE,"af930993-f983-4d4b-806c-d5d714f01deb")}),-1.0]])]});
            var Q2;
            Q2=makeQuery(id+"F12.imprint","IMPRINT",FACE,{"disambiguationData":[TD([[makeQuery(id+"F12.imprint","IMPRINT",EDGE,{"derivedFrom":sQuery(id+"F12.wireOp",EDGE,"544cc5c5-56e9-462e-aa7d-0e891712fb88")}),-1.0]])]});
            var Q3;
            Q3=makeQuery(id+"F12.imprint","IMPRINT",FACE,{"disambiguationData":[TD([[makeQuery(id+"F12.imprint","IMPRINT",EDGE,{"derivedFrom":sQuery(id+"F12.wireOp",EDGE,"a7fd36b7-951d-469d-bd4a-abdf8a5abec4")}),-1.0]])]});
            var Q4;
            Q4=makeQuery(id+"F12.imprint","IMPRINT",FACE,{"disambiguationData":[TD([[makeQuery(id+"F12.imprint","IMPRINT",EDGE,{"derivedFrom":sQuery(id+"F12.wireOp",EDGE,"db4000d2-28b7-4ce0-b6f8-efe2c8e47721")}),-1.0]])]});
            var Q5;
            Q5=makeQuery(id+"F12.imprint","IMPRINT",FACE,{"disambiguationData":[TD([[makeQuery(id+"F12.imprint","IMPRINT",EDGE,{"derivedFrom":sQuery(id+"F12.wireOp",EDGE,"6fd45c98-9014-41e2-a4b9-07c20c1fc8f4")}),-1.0]])]});
            var Q6;
            Q6=makeQuery(id+"F12.imprint","IMPRINT",FACE,{"disambiguationData":[TD([[makeQuery(id+"F12.imprint","IMPRINT",EDGE,{"derivedFrom":sQuery(id+"F12.wireOp",EDGE,"0217be3f-f015-4376-87de-3fac7a7125e00.MirrorCS")}),1.0]])]});
            var Q7;
            Q7=makeQuery(id+"F12.imprint","IMPRINT",FACE,{"disambiguationData":[TD([[makeQuery(id+"F12.imprint","IMPRINT",EDGE,{"derivedFrom":sQuery(id+"F12.wireOp",EDGE,"3a05cbfe-0b2f-41ad-9fce-b7c3e8f461170.MirrorCS")}),1.0]])]});
            var Q8;
            Q8=makeQuery(id+"F12.imprint","IMPRINT",FACE,{"disambiguationData":[TD([[makeQuery(id+"F12.imprint","IMPRINT",EDGE,{"derivedFrom":sQuery(id+"F12.wireOp",EDGE,"686798c7-8504-4800-9966-571d6854760d0.MirrorCS")}),1.0]])]});
            var Q9;
            Q9=makeQuery(id+"F12.imprint","IMPRINT",FACE,{"disambiguationData":[TD([[makeQuery(id+"F12.imprint","IMPRINT",EDGE,{"derivedFrom":sQuery(id+"F12.wireOp",EDGE,"ee1293b9-60a1-4feb-baa6-848b5ec06ea80.MirrorCS")}),1.0]])]});
            var Q10;
            Q10=makeQuery(id+"F12.imprint","IMPRINT",FACE,{"disambiguationData":[TD([[makeQuery(id+"F12.imprint","IMPRINT",EDGE,{"derivedFrom":sQuery(id+"F12.wireOp",EDGE,"E89")}),-1.0]])]});
            var Q11;
            Q11=makeQuery(id+"F12.imprint","IMPRINT",FACE,{"disambiguationData":[TD([[makeQuery(id+"F12.imprint","IMPRINT",EDGE,{"derivedFrom":sQuery(id+"F12.wireOp",EDGE,"E78")}),-1.0]])]});
            var Q12;
            Q12=makeQuery(id+"F12.imprint","IMPRINT",FACE,{"disambiguationData":[TD([[makeQuery(id+"F12.imprint","IMPRINT",EDGE,{"derivedFrom":sQuery(id+"F12.wireOp",EDGE,"E84")}),-1.0]])]});
            var Q13;
            Q13=makeQuery(id+"F12.imprint","IMPRINT",FACE,{"disambiguationData":[TD([[makeQuery(id+"F12.imprint","IMPRINT",EDGE,{"derivedFrom":sQuery(id+"F12.wireOp",EDGE,"E81")}),-1.0]])]});
            var Q14;
            Q14=makeQuery(id+"F12.imprint","IMPRINT",FACE,{"disambiguationData":[TD([[makeQuery(id+"F12.imprint","IMPRINT",EDGE,{"derivedFrom":sQuery(id+"F12.wireOp",EDGE,"E92")}),-1.0]])]});
            var Q15;
            Q15=makeQuery(id+"F12.imprint","IMPRINT",FACE,{"disambiguationData":[TD([[makeQuery(id+"F12.imprint","IMPRINT",EDGE,{"derivedFrom":sQuery(id+"F12.wireOp",EDGE,"E121")}),-1.0]])]});
            var Q16;
            Q16=makeQuery(id+"F12.imprint","IMPRINT",FACE,{"disambiguationData":[TD([[makeQuery(id+"F12.imprint","IMPRINT",EDGE,{"derivedFrom":sQuery(id+"F12.wireOp",EDGE,"E111")}),-1.0]])]});
            var Q17;
            Q17=makeQuery(id+"F12.imprint","IMPRINT",FACE,{"disambiguationData":[TD([[makeQuery(id+"F12.imprint","IMPRINT",EDGE,{"derivedFrom":sQuery(id+"F12.wireOp",EDGE,"E105")}),-1.0]])]});
            var Q18;
            Q18=makeQuery(id+"F12.imprint","IMPRINT",FACE,{"disambiguationData":[TD([[makeQuery(id+"F12.imprint","IMPRINT",EDGE,{"derivedFrom":sQuery(id+"F12.wireOp",EDGE,"E108")}),-1.0]])]});
            var Q19;
            Q19=makeQuery(id+"F12.imprint","IMPRINT",FACE,{"disambiguationData":[TD([[makeQuery(id+"F12.imprint","IMPRINT",EDGE,{"derivedFrom":sQuery(id+"F12.wireOp",EDGE,"E114")}),-1.0]])]});
            var Q20;
            Q20=makeQuery(id+"F12.imprint","IMPRINT",FACE,{"disambiguationData":[TD([[makeQuery(id+"F12.imprint","IMPRINT",EDGE,{"derivedFrom":sQuery(id+"F12.wireOp",EDGE,"E98")}),-1.0]])]});
            var Q21;
            Q21=makeQuery(id+"F12.imprint","IMPRINT",FACE,{"disambiguationData":[TD([[makeQuery(id+"F12.imprint","IMPRINT",EDGE,{"derivedFrom":sQuery(id+"F12.wireOp",EDGE,"E95")}),-1.0]])]});
            var Q22;
            Q22=makeQuery(id+"F12.imprint","IMPRINT",FACE,{"disambiguationData":[TD([[makeQuery(id+"F12.imprint","IMPRINT",EDGE,{"derivedFrom":sQuery(id+"F12.wireOp",EDGE,"E101")}),-1.0]])]});
            var Q23;
            Q23=makeQuery(id+"F12.imprint","IMPRINT",FACE,{"disambiguationData":[TD([[makeQuery(id+"F12.imprint","IMPRINT",EDGE,{"derivedFrom":sQuery(id+"F12.wireOp",EDGE,"E118")}),-1.0]])]});
            var Q24;
            Q24=makeQuery(id+"F12.imprint","IMPRINT",FACE,{"disambiguationData":[TD([[makeQuery(id+"F12.imprint","IMPRINT",EDGE,{"derivedFrom":sQuery(id+"F12.wireOp",EDGE,"E152")}),-1.0]])]});
            var Q25;
            Q25=makeQuery(id+"F12.imprint","IMPRINT",FACE,{"disambiguationData":[TD([[makeQuery(id+"F12.imprint","IMPRINT",EDGE,{"derivedFrom":sQuery(id+"F12.wireOp",EDGE,"E146")}),-1.0]])]});
            var Q26;
            Q26=makeQuery(id+"F12.imprint","IMPRINT",FACE,{"disambiguationData":[TD([[makeQuery(id+"F12.imprint","IMPRINT",EDGE,{"derivedFrom":sQuery(id+"F12.wireOp",EDGE,"E140")}),-1.0]])]});
            var Q27;
            Q27=makeQuery(id+"F12.imprint","IMPRINT",FACE,{"disambiguationData":[TD([[makeQuery(id+"F12.imprint","IMPRINT",EDGE,{"derivedFrom":sQuery(id+"F12.wireOp",EDGE,"E143")}),-1.0]])]});
            var Q28;
            Q28=makeQuery(id+"F12.imprint","IMPRINT",FACE,{"disambiguationData":[TD([[makeQuery(id+"F12.imprint","IMPRINT",EDGE,{"derivedFrom":sQuery(id+"F12.wireOp",EDGE,"E149")}),-1.0]])]});
            var Q29;
            Q29=makeQuery(id+"F12.imprint","IMPRINT",FACE,{"disambiguationData":[TD([[makeQuery(id+"F12.imprint","IMPRINT",EDGE,{"derivedFrom":sQuery(id+"F12.wireOp",EDGE,"E133")}),-1.0]])]});
            var Q30;
            Q30=makeQuery(id+"F12.imprint","IMPRINT",FACE,{"disambiguationData":[TD([[makeQuery(id+"F12.imprint","IMPRINT",EDGE,{"derivedFrom":sQuery(id+"F12.wireOp",EDGE,"E127")}),-1.0]])]});
            var Q31;
            Q31=makeQuery(id+"F12.imprint","IMPRINT",FACE,{"disambiguationData":[TD([[makeQuery(id+"F12.imprint","IMPRINT",EDGE,{"derivedFrom":sQuery(id+"F12.wireOp",EDGE,"E124")}),-1.0]])]});
            var Q32;
            Q32=makeQuery(id+"F12.imprint","IMPRINT",FACE,{"disambiguationData":[TD([[makeQuery(id+"F12.imprint","IMPRINT",EDGE,{"derivedFrom":sQuery(id+"F12.wireOp",EDGE,"E130")}),-1.0]])]});
            var Q33;
            Q33=makeQuery(id+"F12.imprint","IMPRINT",FACE,{"disambiguationData":[TD([[makeQuery(id+"F12.imprint","IMPRINT",EDGE,{"derivedFrom":sQuery(id+"F12.wireOp",EDGE,"E137")}),-1.0]])]});
            extrude(context, id + "F14", {"entities" : qUnion([Q0, Q1, Q2, Q3, Q4, Q5, Q6, Q7, Q8, Q9, Q10, Q11, Q12, Q13, Q14, Q15, Q16, Q17, Q18, Q19, Q20, Q21, Q22, Q23, Q24, Q25, Q26, Q27, Q28, Q29, Q30, Q31, Q32, Q33]), "operationType" : NewBodyOperationType.REMOVE, "depth" : 3 * mm, "offsetDistance" : 25 * mm});
        }
    });
